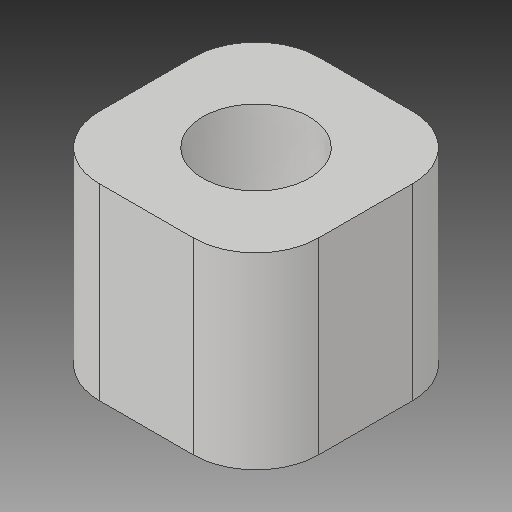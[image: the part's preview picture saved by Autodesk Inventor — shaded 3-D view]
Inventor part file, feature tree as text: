
AUTODESK INVENTOR PART (.ipt)
format: ipt  version: 2019 (Build 230136000, 136)  size: 99,328 bytes
history: native  units: mm
features: extrude x1, fillet x1, sketch x1
ambient origin geometry x8: Origin, YZ Plane, XZ Plane, XY Plane, X Axis, Y Axis, Z Axis, Center Point
bodies: Solid1 (feature_tree)
feature tree (3):
  extrude  "Extrusion1"  Depth=7.0mm
  fillet  "Fillet1"  Radius=6.0mm
  sketch  "Sketch1"  dims[d0=3.4mm d1=7.0mm d2=6.0mm d3=0.0mm d4=2.0mm]
